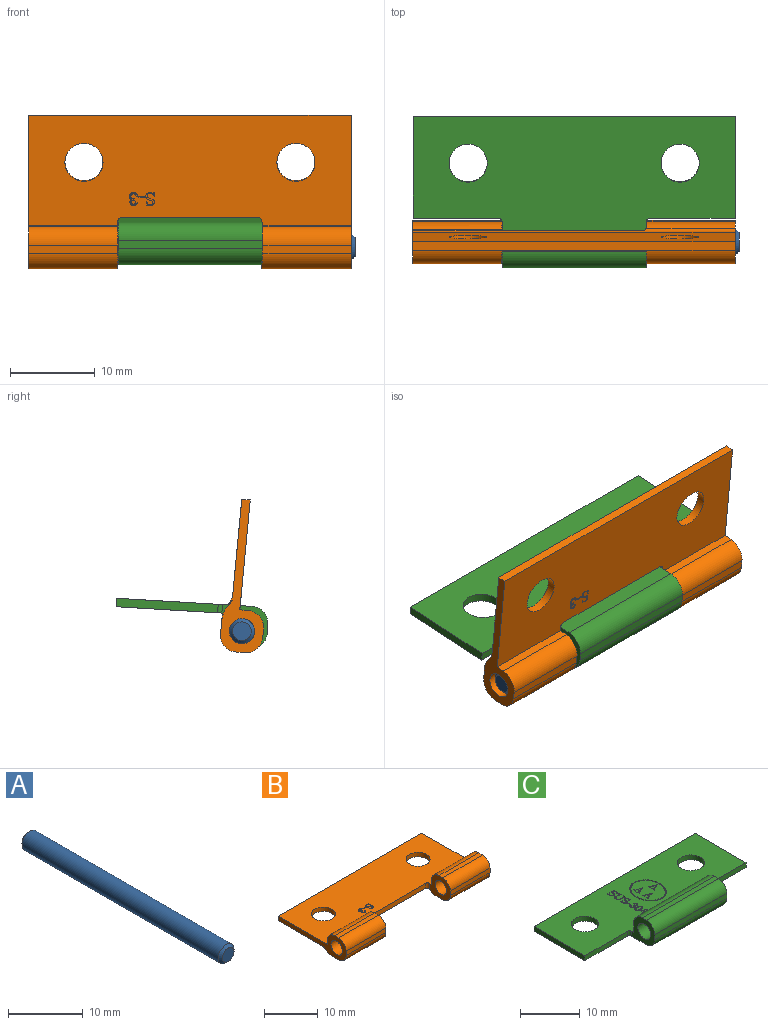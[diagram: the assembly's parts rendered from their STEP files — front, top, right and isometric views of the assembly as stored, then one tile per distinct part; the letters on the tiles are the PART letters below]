
ASSEMBLY  parts=3 mates=2
PART A: 5 faces, bbox 3x38x3 mm
  f0: cone r=1.3mm half-angle=45deg, axis (0,-1,0), area 4.6mm2, adj f1,f2
  f1: cylinder r=1.5mm len=37.2mm, axis (0,1,0), area 350.6mm2, adj f0,f3
  f2: plane 2.2x2.2mm, normal (0,1,0), area 3.8mm2, adj f0
  f3: cone r=1.3mm half-angle=45deg, axis (0,1,0), area 4.6mm2, adj f1,f4
  f4: plane 2.2x2.2mm, normal (0,-1,0), area 3.8mm2, adj f3
PART B: 86 faces, bbox 38x18x5 mm
  f0: extruded ~0.2x0.06mm, area 0mm2, adj f1,f7,f8,f83
  f1: plane 0.2x0.06mm, normal (-1,0,0), area 0mm2, adj f0,f2,f8,f83
  f2: extruded ~0.2x0.06mm, area 0mm2, adj f1,f3,f8,f83
  f3: plane 0.61x0.2mm, normal (0,-1,0), area 0.1mm2, adj f2,f4,f8,f83
  f4: extruded ~0.2x0.05mm, area 0mm2, adj f3,f5,f8,f83
  f5: plane 0.2x0.06mm, normal (1,0,0), area 0mm2, adj f4,f6,f8,f83
  f6: extruded ~0.2x0.05mm, area 0mm2, adj f5,f7,f8,f83
  f7: plane 0.63x0.2mm, normal (0,1,0), area 0.1mm2, adj f0,f6,f8,f83
  f8: plane 0.72x0.15mm, normal (0,0,1), area 0.1mm2, adj f0,f1,f2,f3,f4,f5,f6,f7
  f9: extruded ~0.33x0.2mm, area 0.1mm2, adj f10,f34,f35,f83
  f10: extruded ~0.47x0.38mm, area 0.1mm2, adj f9,f11,f35,f83
  f11: extruded ~0.44x0.42mm, area 0.1mm2, adj f10,f12,f35,f83
  f12: extruded ~0.42x0.36mm, area 0.1mm2, adj f11,f13,f35,f83
  f13: extruded ~0.33x0.31mm, area 0.1mm2, adj f12,f14,f35,f83
  f14: extruded ~0.49x0.44mm, area 0.1mm2, adj f13,f15,f35,f83
  f15: extruded ~0.2x0.03mm, area 0mm2, adj f14,f16,f35,f83
  f16: extruded ~0.2x0.02mm, area 0mm2, adj f15,f17,f35,f83
  f17: extruded ~0.48x0.2mm, area 0.1mm2, adj f16,f18,f35,f83
  f18: extruded ~0.2x0.04mm, area 0mm2, adj f17,f19,f35,f83
  f19: cylinder r=0.16mm len=0.2mm, axis (0,0,1), area 0mm2, adj f18,f20,f35,f83
  f20: extruded ~0.39x0.2mm, area 0.1mm2, adj f19,f21,f35,f83
  f21: extruded ~0.51x0.46mm, area 0.2mm2, adj f20,f22,f35,f83
  f22: extruded ~0.46x0.44mm, area 0.1mm2, adj f21,f23,f35,f83
  f23: extruded ~0.31x0.2mm, area 0.1mm2, adj f22,f24,f35,f83
  f24: extruded ~0.2x0.17mm, area 0mm2, adj f23,f25,f35,f83
  f25: extruded ~0.28x0.26mm, area 0.1mm2, adj f24,f26,f35,f83
  f26: extruded ~0.26x0.2mm, area 0.1mm2, adj f25,f27,f35,f83
  f27: cylinder r=0.62mm len=0.25mm, axis (0,0,1), area 0.1mm2, adj f26,f28,f35,f83
  f28: extruded ~0.2x0.02mm, area 0mm2, adj f27,f29,f35,f83
  f29: extruded ~0.2x0.03mm, area 0mm2, adj f28,f30,f35,f83
  f30: plane 0.21x0.2mm, normal (0.99,0.13,0), area 0mm2, adj f29,f31,f35,f83
  f31: bspline ~0.2x0.16mm, area 0mm2, adj f30,f32,f35,f83
  f32: extruded ~0.2x0.02mm, area 0mm2, adj f31,f33,f35,f83
  f33: extruded ~0.2x0.03mm, area 0mm2, adj f32,f34,f35,f83
  f34: extruded ~0.2x0.06mm, area 0mm2, adj f9,f33,f35,f83
  f35: plane 1.52x1.04mm, normal (0,0,1), area 0.5mm2, adj f9,f10,f11,f12,f13,f14,f15,f16
  f36: extruded ~0.48x0.42mm, area 0.1mm2, adj f37,f52,f53,f83
  f37: extruded ~0.51x0.47mm, area 0.2mm2, adj f36,f38,f53,f83
  f38: extruded ~0.37x0.28mm, area 0.1mm2, adj f37,f39,f53,f83
  f39: extruded ~0.3x0.21mm, area 0.1mm2, adj f38,f40,f53,f83
  f40: extruded ~0.44x0.39mm, area 0.1mm2, adj f39,f41,f53,f83
  f41: extruded ~0.45x0.39mm, area 0.1mm2, adj f40,f42,f53,f83
  f42: plane 0.2x0.18mm, normal (-0.18,-0.98,0), area 0mm2, adj f41,f43,f53,f83
  f43: extruded ~0.27x0.27mm, area 0.1mm2, adj f42,f44,f53,f83
  f44: extruded ~0.25x0.23mm, area 0.1mm2, adj f43,f45,f53,f83
  f45: extruded ~0.31x0.25mm, area 0.1mm2, adj f44,f46,f53,f83
  f46: cylinder r=0.38mm len=0.2mm, axis (0,0,1), area 0mm2, adj f45,f47,f53,f83
  f47: plane 0.2x0.16mm, normal (-0.99,0.12,0), area 0mm2, adj f46,f48,f53,f83
  f48: extruded ~0.2x0.13mm, area 0mm2, adj f47,f49,f53,f83
  f49: extruded ~0.29x0.29mm, area 0.1mm2, adj f48,f50,f53,f83
  f50: extruded ~0.31x0.31mm, area 0.1mm2, adj f49,f51,f53,f83
  f51: extruded ~0.3x0.29mm, area 0.1mm2, adj f50,f52,f53,f83
  f52: plane 0.2x0.18mm, normal (-0.13,0.99,0), area 0mm2, adj f36,f51,f53,f83
  f53: plane 1.53x0.98mm, normal (0,0,1), area 0.6mm2, adj f36,f37,f38,f39,f40,f41,f42,f43
  f54: cylinder r=3mm len=10.5mm, axis (1,0,0), area 22.1mm2, adj f55,f56,f57,f72,f81
  f55: plane 5.5x5mm, normal (1,0,0), area 15.9mm2, adj f54,f56,f68,f70,f72,f73,f75,f76
  f56: cylinder r=0.5mm len=1.32mm, axis (0,0,-1), area 0.9mm2, adj f54,f55,f57,f64,f83
  f57: cylinder r=2mm len=11mm, axis (1,0,0), area 5.9mm2, adj f54,f56,f64,f81
  f58: cylinder r=3mm len=10.5mm, axis (1,0,0), area 20.3mm2, adj f59,f60,f61,f63,f69
  f59: plane 10.5x1.73mm, normal (0,0,-1), area 18.2mm2, adj f58,f60,f69,f80
  f60: plane 18x5mm, normal (1,0,0), area 28.7mm2, adj f58,f59,f61,f62,f67,f71,f74,f77
  f61: cylinder r=2mm len=38mm, axis (-1,0,0), area 34.3mm2, adj f58,f60,f62,f63,f64,f81
  f62: plane 38x11.27mm, normal (0,0,-1), area 396.4mm2, adj f60,f61,f65,f66,f81,f84
  f63: cylinder r=0.5mm len=1.42mm, axis (0,0,-1), area 1mm2, adj f58,f61,f64,f69,f83
  f64: plane 27x1.14mm, normal (0,-1,0), area 19.7mm2, adj f56,f57,f61,f63,f81,f83
  f65: cylinder r=2.25mm len=4.5mm, axis (0,0,1), area 14.1mm2, adj f62,f83
  f66: cylinder r=2.25mm len=4.5mm, axis (0,0,1), area 14.1mm2, adj f62,f83
  f67: cylinder r=1.5mm len=10.5mm, axis (1,0,0), area 99mm2, adj f60,f69
  f68: cylinder r=1.5mm len=10.5mm, axis (1,0,0), area 99mm2, adj f55,f81
  f69: plane 5.5x5mm, normal (-1,0,0), area 16mm2, adj f58,f59,f63,f67,f71,f74,f77,f80
  f70: plane 10.5x1mm, normal (0,1,0), area 10.5mm2, adj f55,f73,f81,f83
  f71: plane 10.5x1mm, normal (0,1,0), area 10.5mm2, adj f60,f69,f74,f83
  f72: plane 10.5x1.6mm, normal (0,0,-1), area 16.8mm2, adj f54,f55,f75,f81
  f73: cylinder r=2mm len=10.5mm, axis (-1,0,0), area 33mm2, adj f55,f70,f76,f81
  f74: cylinder r=2mm len=10.5mm, axis (-1,0,0), area 33mm2, adj f60,f69,f71,f77
  f75: cylinder r=2mm len=10.5mm, axis (-1,0,0), area 33mm2, adj f55,f72,f78,f81
  f76: plane 10.5x1mm, normal (0,0,1), area 10.5mm2, adj f55,f73,f79,f81
  f77: plane 10.5x1mm, normal (0,0,1), area 10.5mm2, adj f60,f69,f74,f82
  f78: plane 10.5x1mm, normal (0,-1,0), area 10.5mm2, adj f55,f75,f79,f81
  f79: cylinder r=2mm len=10.5mm, axis (1,0,0), area 33mm2, adj f55,f76,f78,f81
  f80: cylinder r=2mm len=10.5mm, axis (-1,0,0), area 33mm2, adj f59,f60,f69,f85
  f81: plane 18x5mm, normal (-1,0,0), area 28.6mm2, adj f54,f57,f61,f62,f64,f68,f70,f72
  f82: cylinder r=2mm len=10.5mm, axis (1,0,0), area 33mm2, adj f60,f69,f77,f85
  f83: plane 38x13mm, normal (0,0,1), area 444.2mm2, adj f0,f1,f2,f3,f4,f5,f6,f7
  f84: plane 38x1mm, normal (0,1,0), area 38mm2, adj f60,f62,f81,f83
  f85: plane 10.5x1mm, normal (0,-1,0), area 10.5mm2, adj f60,f69,f80,f82
PART C: 246 faces, bbox 38.1x18.1x5.1 mm
  f0: extruded ~6.17x5.24mm, area 3.6mm2, adj f2,f221
  f1: extruded ~6.57x5.64mm, area 3.8mm2, adj f2,f3
  f2: plane 6.66x5.73mm, normal (0,0,1), area 3.7mm2, adj f0,f1
  f3: plane 38x13mm, normal (0,0,1), area 408mm2, adj f1,f7,f8,f9,f10,f11,f12,f13
  f4: plane 0.68x0.47mm, normal (0.57,0.82,0), area 0.2mm2, adj f5,f6,f18,f243
  f5: plane 0.47x0.2mm, normal (-1,0,0), area 0.1mm2, adj f4,f6,f18,f243
  f6: plane 0.68x0.2mm, normal (0,-1,0), area 0.1mm2, adj f4,f5,f18,f243
  f7: plane 0.2x0.18mm, normal (1,0,0), area 0mm2, adj f3,f8,f17,f18
  f8: plane 0.36x0.2mm, normal (0,1,0), area 0.1mm2, adj f3,f7,f9,f18
  f9: plane 0.2x0.2mm, normal (1,0,0), area 0mm2, adj f3,f8,f10,f18
  f10: plane 0.2x0.17mm, normal (0,1,0), area 0mm2, adj f3,f9,f11,f18
  f11: plane 0.2x0.2mm, normal (-1,0,0), area 0mm2, adj f3,f10,f12,f18
  f12: plane 0.97x0.2mm, normal (0,1,0), area 0.2mm2, adj f3,f11,f13,f18
  f13: plane 0.2x0.15mm, normal (-1,0,0), area 0mm2, adj f3,f12,f14,f18
  f14: plane 0.97x0.68mm, normal (-0.58,-0.82,0), area 0.2mm2, adj f3,f13,f15,f18
  f15: plane 0.2x0.17mm, normal (0,-1,0), area 0mm2, adj f3,f14,f16,f18
  f16: plane 0.65x0.2mm, normal (1,0,0), area 0.1mm2, adj f3,f15,f17,f18
  f17: plane 0.36x0.2mm, normal (0,-1,0), area 0.1mm2, adj f3,f7,f16,f18
  f18: plane 1.5x1.04mm, normal (0,0,1), area 0.6mm2, adj f4,f5,f6,f7,f8,f9,f10,f11
  f19: extruded ~0.61x0.3mm, area 0.2mm2, adj f20,f23,f29,f225
  f20: extruded ~0.61x0.3mm, area 0.2mm2, adj f19,f21,f29,f225
  f21: cylinder r=0.24mm len=0.2mm, axis (0,0,-1), area 0mm2, adj f20,f22,f29,f225
  f22: extruded ~0.51x0.2mm, area 0.1mm2, adj f21,f23,f29,f225
  f23: extruded ~0.61x0.3mm, area 0.2mm2, adj f19,f22,f29,f225
  f24: extruded ~0.61x0.2mm, area 0.1mm2, adj f3,f25,f28,f29
  f25: extruded ~0.34x0.2mm, area 0.1mm2, adj f3,f24,f26,f29
  f26: extruded ~0.77x0.49mm, area 0.2mm2, adj f3,f25,f27,f29
  f27: extruded ~0.77x0.49mm, area 0.2mm2, adj f3,f26,f28,f29
  f28: extruded ~0.77x0.49mm, area 0.2mm2, adj f3,f24,f27,f29
  f29: plane 1.53x0.98mm, normal (0,0,1), area 0.6mm2, adj f19,f20,f21,f22,f23,f24,f25,f26
  f30: extruded ~0.2x0.06mm, area 0mm2, adj f3,f31,f37,f38
  f31: plane 0.2x0.06mm, normal (0,-1,0), area 0mm2, adj f3,f30,f32,f38
  f32: extruded ~0.2x0.06mm, area 0mm2, adj f3,f31,f33,f38
  f33: plane 0.61x0.2mm, normal (1,0,0), area 0.1mm2, adj f3,f32,f34,f38
  f34: extruded ~0.2x0.05mm, area 0mm2, adj f3,f33,f35,f38
  f35: plane 0.2x0.06mm, normal (0,1,0), area 0mm2, adj f3,f34,f36,f38
  f36: extruded ~0.2x0.05mm, area 0mm2, adj f3,f35,f37,f38
  f37: plane 0.63x0.2mm, normal (-1,0,0), area 0.1mm2, adj f3,f30,f36,f38
  f38: plane 0.72x0.15mm, normal (0,0,1), area 0.1mm2, adj f30,f31,f32,f33,f34,f35,f36,f37
  f39: extruded ~0.2x0.05mm, area 0mm2, adj f3,f40,f57,f58
  f40: extruded ~0.2x0.04mm, area 0mm2, adj f3,f39,f41,f58
  f41: extruded ~0.61x0.2mm, area 0.1mm2, adj f3,f40,f42,f58
  f42: plane 0.31x0.2mm, normal (-0.02,-1,0), area 0.1mm2, adj f3,f41,f43,f58
  f43: extruded ~0.57x0.54mm, area 0.2mm2, adj f3,f42,f44,f58
  f44: extruded ~0.93x0.63mm, area 0.3mm2, adj f3,f43,f45,f58
  f45: extruded ~0.53x0.2mm, area 0.1mm2, adj f3,f44,f46,f58
  f46: extruded ~0.2x0.03mm, area 0mm2, adj f3,f45,f47,f58
  f47: extruded ~0.2x0.03mm, area 0mm2, adj f3,f46,f48,f58
  f48: plane 0.45x0.2mm, normal (-1,0,0), area 0.1mm2, adj f3,f47,f49,f58
  f49: extruded ~0.2x0.06mm, area 0mm2, adj f3,f48,f50,f58
  f50: extruded ~0.2x0.04mm, area 0mm2, adj f3,f49,f51,f58
  f51: extruded ~0.42x0.21mm, area 0.1mm2, adj f3,f50,f52,f58
  f52: extruded ~0.95x0.47mm, area 0.2mm2, adj f3,f51,f53,f58
  f53: extruded ~0.8x0.45mm, area 0.2mm2, adj f3,f52,f54,f58
  f54: extruded ~0.56x0.2mm, area 0.1mm2, adj f3,f53,f55,f58
  f55: extruded ~0.2x0.04mm, area 0mm2, adj f3,f54,f56,f58
  f56: extruded ~0.2x0.05mm, area 0mm2, adj f3,f55,f57,f58
  f57: plane 0.57x0.2mm, normal (-1,0,0), area 0.1mm2, adj f3,f39,f56,f58
  f58: plane 1.64x1.5mm, normal (0,0,1), area 0.5mm2, adj f39,f40,f41,f42,f43,f44,f45,f46
  f59: bspline ~0.2x0.17mm, area 0mm2, adj f60,f63,f88,f224
  f60: plane 0.32x0.2mm, normal (-1,0.02,0), area 0.1mm2, adj f59,f61,f88,f224
  f61: extruded ~0.31x0.2mm, area 0.1mm2, adj f60,f62,f88,f224
  f62: extruded ~0.31x0.2mm, area 0.1mm2, adj f61,f63,f88,f224
  f63: extruded ~0.62x0.25mm, area 0.1mm2, adj f59,f62,f88,f224
  f64: extruded ~0.72x0.29mm, area 0.2mm2, adj f65,f87,f88,f221
  f65: extruded ~0.75x0.41mm, area 0.2mm2, adj f64,f66,f88,f221
  f66: extruded ~0.2x0.03mm, area 0mm2, adj f65,f67,f88,f221
  f67: extruded ~0.2x0.04mm, area 0mm2, adj f66,f68,f88,f221
  f68: extruded ~0.25x0.2mm, area 0.1mm2, adj f67,f69,f88,f221
  f69: plane 0.22x0.2mm, normal (1,-0.03,0), area 0mm2, adj f68,f70,f88,f221
  f70: extruded ~0.2x0.02mm, area 0mm2, adj f69,f71,f88,f221
  f71: extruded ~0.2x0.04mm, area 0mm2, adj f70,f72,f88,f221
  f72: extruded ~0.2x0.17mm, area 0mm2, adj f71,f73,f88,f221
  f73: extruded ~0.4x0.2mm, area 0.1mm2, adj f72,f74,f88,f221
  f74: plane 0.53x0.2mm, normal (1,0.01,0), area 0.1mm2, adj f73,f75,f88,f221
  f75: plane 0.2x0.2mm, normal (0.32,-0.95,0), area 0mm2, adj f74,f76,f88,f221
  f76: extruded ~0.24x0.2mm, area 0.1mm2, adj f75,f77,f88,f221
  f77: extruded ~0.2x0.17mm, area 0mm2, adj f76,f78,f88,f221
  f78: extruded ~0.2x0.03mm, area 0mm2, adj f77,f79,f88,f221
  f79: extruded ~0.2x0.04mm, area 0mm2, adj f78,f80,f88,f221
  f80: extruded ~0.32x0.2mm, area 0.1mm2, adj f79,f81,f88,f221
  f81: extruded ~0.26x0.2mm, area 0.1mm2, adj f80,f82,f88,f221
  f82: plane 0.2x0.02mm, normal (1,-0.08,0), area 0mm2, adj f81,f83,f88,f221
  f83: extruded ~0.2x0.02mm, area 0mm2, adj f82,f84,f88,f221
  f84: extruded ~0.2x0.04mm, area 0mm2, adj f83,f85,f88,f221
  f85: extruded ~0.59x0.37mm, area 0.1mm2, adj f84,f86,f88,f221
  f86: extruded ~0.88x0.35mm, area 0.2mm2, adj f85,f87,f88,f221
  f87: plane 0.2x0.05mm, normal (-1,0,0), area 0mm2, adj f64,f86,f88,f221
  f88: plane 1.54x1.52mm, normal (0,0,1), area 0.5mm2, adj f59,f60,f61,f62,f63,f64,f65,f66
  f89: bspline ~0.2x0.17mm, area 0mm2, adj f90,f93,f118,f223
  f90: plane 0.32x0.2mm, normal (-1,0.02,0), area 0.1mm2, adj f89,f91,f118,f223
  f91: extruded ~0.31x0.2mm, area 0.1mm2, adj f90,f92,f118,f223
  f92: extruded ~0.31x0.2mm, area 0.1mm2, adj f91,f93,f118,f223
  f93: extruded ~0.62x0.25mm, area 0.1mm2, adj f89,f92,f118,f223
  f94: extruded ~0.72x0.29mm, area 0.2mm2, adj f95,f117,f118,f221
  f95: extruded ~0.75x0.41mm, area 0.2mm2, adj f94,f96,f118,f221
  f96: extruded ~0.2x0.03mm, area 0mm2, adj f95,f97,f118,f221
  f97: extruded ~0.2x0.04mm, area 0mm2, adj f96,f98,f118,f221
  f98: extruded ~0.25x0.2mm, area 0.1mm2, adj f97,f99,f118,f221
  f99: plane 0.22x0.2mm, normal (1,-0.03,0), area 0mm2, adj f98,f100,f118,f221
  f100: extruded ~0.2x0.02mm, area 0mm2, adj f99,f101,f118,f221
  f101: extruded ~0.2x0.04mm, area 0mm2, adj f100,f102,f118,f221
  f102: extruded ~0.2x0.17mm, area 0mm2, adj f101,f103,f118,f221
  f103: extruded ~0.4x0.2mm, area 0.1mm2, adj f102,f104,f118,f221
  f104: plane 0.53x0.2mm, normal (1,0.01,0), area 0.1mm2, adj f103,f105,f118,f221
  f105: plane 0.2x0.2mm, normal (0.32,-0.95,0), area 0mm2, adj f104,f106,f118,f221
  f106: extruded ~0.24x0.2mm, area 0.1mm2, adj f105,f107,f118,f221
  f107: extruded ~0.2x0.17mm, area 0mm2, adj f106,f108,f118,f221
  f108: extruded ~0.2x0.03mm, area 0mm2, adj f107,f109,f118,f221
  f109: extruded ~0.2x0.04mm, area 0mm2, adj f108,f110,f118,f221
  f110: extruded ~0.32x0.2mm, area 0.1mm2, adj f109,f111,f118,f221
  f111: extruded ~0.26x0.2mm, area 0.1mm2, adj f110,f112,f118,f221
  f112: plane 0.2x0.02mm, normal (1,-0.08,0), area 0mm2, adj f111,f113,f118,f221
  f113: extruded ~0.2x0.02mm, area 0mm2, adj f112,f114,f118,f221
  f114: extruded ~0.2x0.04mm, area 0mm2, adj f113,f115,f118,f221
  f115: extruded ~0.59x0.37mm, area 0.1mm2, adj f114,f116,f118,f221
  f116: extruded ~0.88x0.35mm, area 0.2mm2, adj f115,f117,f118,f221
  f117: plane 0.2x0.05mm, normal (-1,0,0), area 0mm2, adj f94,f116,f118,f221
  f118: plane 1.54x1.52mm, normal (0,0,1), area 0.5mm2, adj f89,f90,f91,f92,f93,f94,f95,f96
  f119: bspline ~0.2x0.17mm, area 0mm2, adj f120,f123,f148,f222
  f120: plane 0.32x0.2mm, normal (-1,0.02,0), area 0.1mm2, adj f119,f121,f148,f222
  f121: extruded ~0.31x0.2mm, area 0.1mm2, adj f120,f122,f148,f222
  f122: extruded ~0.31x0.2mm, area 0.1mm2, adj f121,f123,f148,f222
  f123: extruded ~0.62x0.25mm, area 0.1mm2, adj f119,f122,f148,f222
  f124: extruded ~0.72x0.29mm, area 0.2mm2, adj f125,f147,f148,f221
  f125: extruded ~0.75x0.41mm, area 0.2mm2, adj f124,f126,f148,f221
  f126: extruded ~0.2x0.03mm, area 0mm2, adj f125,f127,f148,f221
  f127: extruded ~0.2x0.04mm, area 0mm2, adj f126,f128,f148,f221
  f128: extruded ~0.25x0.2mm, area 0.1mm2, adj f127,f129,f148,f221
  f129: plane 0.22x0.2mm, normal (1,-0.03,0), area 0mm2, adj f128,f130,f148,f221
  f130: extruded ~0.2x0.02mm, area 0mm2, adj f129,f131,f148,f221
  f131: extruded ~0.2x0.04mm, area 0mm2, adj f130,f132,f148,f221
  f132: extruded ~0.2x0.17mm, area 0mm2, adj f131,f133,f148,f221
  f133: extruded ~0.4x0.2mm, area 0.1mm2, adj f132,f134,f148,f221
  f134: plane 0.53x0.2mm, normal (1,0.01,0), area 0.1mm2, adj f133,f135,f148,f221
  f135: plane 0.2x0.2mm, normal (0.32,-0.95,0), area 0mm2, adj f134,f136,f148,f221
  f136: extruded ~0.24x0.2mm, area 0.1mm2, adj f135,f137,f148,f221
  f137: extruded ~0.2x0.17mm, area 0mm2, adj f136,f138,f148,f221
  f138: extruded ~0.2x0.03mm, area 0mm2, adj f137,f139,f148,f221
  f139: extruded ~0.2x0.04mm, area 0mm2, adj f138,f140,f148,f221
  f140: extruded ~0.32x0.2mm, area 0.1mm2, adj f139,f141,f148,f221
  f141: extruded ~0.26x0.2mm, area 0.1mm2, adj f140,f142,f148,f221
  f142: plane 0.2x0.02mm, normal (1,-0.08,0), area 0mm2, adj f141,f143,f148,f221
  f143: extruded ~0.2x0.02mm, area 0mm2, adj f142,f144,f148,f221
  f144: extruded ~0.2x0.04mm, area 0mm2, adj f143,f145,f148,f221
  f145: extruded ~0.59x0.37mm, area 0.1mm2, adj f144,f146,f148,f221
  f146: extruded ~0.88x0.35mm, area 0.2mm2, adj f145,f147,f148,f221
  f147: plane 0.2x0.05mm, normal (-1,0,0), area 0mm2, adj f124,f146,f148,f221
  f148: plane 1.54x1.52mm, normal (0,0,1), area 0.5mm2, adj f119,f120,f121,f122,f123,f124,f125,f126
  f149: extruded ~0.33x0.2mm, area 0.1mm2, adj f3,f150,f174,f175
  f150: extruded ~0.47x0.38mm, area 0.1mm2, adj f3,f149,f151,f175
  f151: extruded ~0.44x0.42mm, area 0.1mm2, adj f3,f150,f152,f175
  f152: extruded ~0.42x0.36mm, area 0.1mm2, adj f3,f151,f153,f175
  f153: extruded ~0.33x0.31mm, area 0.1mm2, adj f3,f152,f154,f175
  f154: extruded ~0.49x0.44mm, area 0.1mm2, adj f3,f153,f155,f175
  f155: extruded ~0.2x0.03mm, area 0mm2, adj f3,f154,f156,f175
  f156: extruded ~0.2x0.02mm, area 0mm2, adj f3,f155,f157,f175
  f157: extruded ~0.48x0.2mm, area 0.1mm2, adj f3,f156,f158,f175
  f158: extruded ~0.2x0.04mm, area 0mm2, adj f3,f157,f159,f175
  f159: cylinder r=0.16mm len=0.2mm, axis (0,0,1), area 0mm2, adj f3,f158,f160,f175
  f160: extruded ~0.39x0.2mm, area 0.1mm2, adj f3,f159,f161,f175
  f161: extruded ~0.51x0.46mm, area 0.2mm2, adj f3,f160,f162,f175
  f162: extruded ~0.46x0.44mm, area 0.1mm2, adj f3,f161,f163,f175
  f163: extruded ~0.31x0.2mm, area 0.1mm2, adj f3,f162,f164,f175
  f164: extruded ~0.2x0.17mm, area 0mm2, adj f3,f163,f165,f175
  f165: extruded ~0.28x0.26mm, area 0.1mm2, adj f3,f164,f166,f175
  f166: extruded ~0.26x0.2mm, area 0.1mm2, adj f3,f165,f167,f175
  f167: cylinder r=0.62mm len=0.25mm, axis (0,0,1), area 0.1mm2, adj f3,f166,f168,f175
  f168: extruded ~0.2x0.02mm, area 0mm2, adj f3,f167,f169,f175
  f169: extruded ~0.2x0.03mm, area 0mm2, adj f3,f168,f170,f175
  f170: plane 0.21x0.2mm, normal (-0.13,0.99,0), area 0mm2, adj f3,f169,f171,f175
  f171: bspline ~0.2x0.16mm, area 0mm2, adj f3,f170,f172,f175
  f172: extruded ~0.2x0.02mm, area 0mm2, adj f3,f171,f173,f175
  f173: extruded ~0.2x0.03mm, area 0mm2, adj f3,f172,f174,f175
  f174: extruded ~0.2x0.06mm, area 0mm2, adj f3,f149,f173,f175
  f175: plane 1.52x1.04mm, normal (0,0,1), area 0.5mm2, adj f149,f150,f151,f152,f153,f154,f155,f156
  f176: extruded ~0.33x0.2mm, area 0.1mm2, adj f3,f177,f201,f202
  f177: extruded ~0.47x0.38mm, area 0.1mm2, adj f3,f176,f178,f202
  f178: extruded ~0.44x0.42mm, area 0.1mm2, adj f3,f177,f179,f202
  f179: extruded ~0.42x0.36mm, area 0.1mm2, adj f3,f178,f180,f202
  f180: extruded ~0.33x0.31mm, area 0.1mm2, adj f3,f179,f181,f202
  f181: extruded ~0.49x0.44mm, area 0.1mm2, adj f3,f180,f182,f202
  f182: extruded ~0.2x0.03mm, area 0mm2, adj f3,f181,f183,f202
  f183: extruded ~0.2x0.02mm, area 0mm2, adj f3,f182,f184,f202
  f184: extruded ~0.48x0.2mm, area 0.1mm2, adj f3,f183,f185,f202
  f185: extruded ~0.2x0.04mm, area 0mm2, adj f3,f184,f186,f202
  f186: cylinder r=0.16mm len=0.2mm, axis (0,0,1), area 0mm2, adj f3,f185,f187,f202
  f187: extruded ~0.39x0.2mm, area 0.1mm2, adj f3,f186,f188,f202
  f188: extruded ~0.51x0.46mm, area 0.2mm2, adj f3,f187,f189,f202
  f189: extruded ~0.46x0.44mm, area 0.1mm2, adj f3,f188,f190,f202
  f190: extruded ~0.31x0.2mm, area 0.1mm2, adj f3,f189,f191,f202
  f191: extruded ~0.2x0.17mm, area 0mm2, adj f3,f190,f192,f202
  f192: extruded ~0.28x0.26mm, area 0.1mm2, adj f3,f191,f193,f202
  f193: extruded ~0.26x0.2mm, area 0.1mm2, adj f3,f192,f194,f202
  f194: cylinder r=0.62mm len=0.25mm, axis (0,0,1), area 0.1mm2, adj f3,f193,f195,f202
  f195: extruded ~0.2x0.02mm, area 0mm2, adj f3,f194,f196,f202
  f196: extruded ~0.2x0.03mm, area 0mm2, adj f3,f195,f197,f202
  f197: plane 0.21x0.2mm, normal (-0.13,0.99,0), area 0mm2, adj f3,f196,f198,f202
  f198: bspline ~0.2x0.16mm, area 0mm2, adj f3,f197,f199,f202
  f199: extruded ~0.2x0.02mm, area 0mm2, adj f3,f198,f200,f202
  f200: extruded ~0.2x0.03mm, area 0mm2, adj f3,f199,f201,f202
  f201: extruded ~0.2x0.06mm, area 0mm2, adj f3,f176,f200,f202
  f202: plane 1.52x1.04mm, normal (0,0,1), area 0.5mm2, adj f176,f177,f178,f179,f180,f181,f182,f183
  f203: extruded ~0.48x0.42mm, area 0.1mm2, adj f3,f204,f219,f220
  f204: extruded ~0.51x0.47mm, area 0.2mm2, adj f3,f203,f205,f220
  f205: extruded ~0.37x0.28mm, area 0.1mm2, adj f3,f204,f206,f220
  f206: extruded ~0.3x0.21mm, area 0.1mm2, adj f3,f205,f207,f220
  f207: extruded ~0.44x0.39mm, area 0.1mm2, adj f3,f206,f208,f220
  f208: extruded ~0.45x0.39mm, area 0.1mm2, adj f3,f207,f209,f220
  f209: plane 0.2x0.18mm, normal (0.98,-0.18,0), area 0mm2, adj f3,f208,f210,f220
  f210: extruded ~0.27x0.27mm, area 0.1mm2, adj f3,f209,f211,f220
  f211: extruded ~0.25x0.23mm, area 0.1mm2, adj f3,f210,f212,f220
  f212: extruded ~0.31x0.25mm, area 0.1mm2, adj f3,f211,f213,f220
  f213: cylinder r=0.38mm len=0.2mm, axis (0,0,1), area 0mm2, adj f3,f212,f214,f220
  f214: plane 0.2x0.16mm, normal (-0.12,-0.99,0), area 0mm2, adj f3,f213,f215,f220
  f215: extruded ~0.2x0.13mm, area 0mm2, adj f3,f214,f216,f220
  f216: extruded ~0.29x0.29mm, area 0.1mm2, adj f3,f215,f217,f220
  f217: extruded ~0.31x0.31mm, area 0.1mm2, adj f3,f216,f218,f220
  f218: extruded ~0.3x0.29mm, area 0.1mm2, adj f3,f217,f219,f220
  f219: plane 0.2x0.18mm, normal (-0.99,-0.13,0), area 0mm2, adj f3,f203,f218,f220
  f220: plane 1.53x0.98mm, normal (0,0,1), area 0.6mm2, adj f203,f204,f205,f206,f207,f208,f209,f210
  f221: plane 6.26x5.33mm, normal (0,0,1), area 23.5mm2, adj f0,f64,f65,f66,f67,f68,f69,f70
  f222: plane 0.62x0.49mm, normal (0,0,1), area 0.2mm2, adj f119,f120,f121,f122,f123
  f223: plane 0.62x0.49mm, normal (0,0,1), area 0.2mm2, adj f89,f90,f91,f92,f93
  f224: plane 0.62x0.49mm, normal (0,0,1), area 0.2mm2, adj f59,f60,f61,f62,f63
  f225: plane 1.23x0.6mm, normal (0,0,1), area 0.6mm2, adj f19,f20,f21,f22,f23
  f226: cylinder r=0.5mm len=1mm, axis (0,0,-1), area 0.8mm2, adj f3,f227,f234,f240
  f227: plane 5.5x5mm, normal (1,0,0), area 15.9mm2, adj f3,f226,f232,f236,f237,f238,f239,f240
  f228: cylinder r=0.5mm len=1mm, axis (0,0,-1), area 0.8mm2, adj f3,f229,f233,f240
  f229: plane 10x1mm, normal (0,-1,0), area 10mm2, adj f3,f228,f240,f241
  f230: cylinder r=2.25mm len=4.5mm, axis (0,0,1), area 14.1mm2, adj f3,f240
  f231: cylinder r=2.25mm len=4.5mm, axis (0,0,1), area 14.1mm2, adj f3,f240
  f232: cylinder r=1.5mm len=17mm, axis (1,0,0), area 160.2mm2, adj f227,f233
  f233: plane 5.5x5mm, normal (-1,0,0), area 15.9mm2, adj f3,f228,f232,f236,f237,f238,f239,f240
  f234: plane 10x1mm, normal (0,-1,0), area 10mm2, adj f3,f226,f235,f240
  f235: plane 12x1mm, normal (1,0,0), area 12mm2, adj f3,f234,f240,f245
  f236: plane 17x2mm, normal (0,1,0), area 34mm2, adj f3,f227,f233,f237
  f237: cylinder r=2mm len=17mm, axis (-1,0,0), area 53.4mm2, adj f227,f233,f236,f238
  f238: plane 17x1mm, normal (0,0,1), area 17mm2, adj f227,f233,f237,f242
  f239: cylinder r=2mm len=17mm, axis (-1,0,0), area 53.4mm2, adj f227,f233,f240,f244
  f240: plane 38x16mm, normal (0,0,-1), area 492.3mm2, adj f226,f227,f228,f229,f230,f231,f233,f234
  f241: plane 12x1mm, normal (-1,0,0), area 12mm2, adj f3,f229,f240,f245
  f242: cylinder r=2mm len=17mm, axis (1,0,0), area 53.4mm2, adj f227,f233,f238,f244
  f243: plane 0.68x0.47mm, normal (0,0,1), area 0.2mm2, adj f4,f5,f6
  f244: plane 17x1mm, normal (0,-1,0), area 17mm2, adj f227,f233,f239,f242
  f245: plane 38x1mm, normal (0,1,0), area 38mm2, adj f3,f235,f240,f241
PLACE A rot(axis=(0.59,0.59,-0.54),123.2deg) t=(-18.75,-58.26,8.1)mm
PLACE B rot(axis=(1,0,0),95.4deg) t=(-0.24,-56.38,14.81)mm
PLACE C rot(axis=(0,-1,-0.03),180deg) t=(-0.22,-52.45,11.46)mm
MATE revolute B.f67 <-> A.f0  axis (1,0,0) through (-19.24,-58.26,8.1)mm
MATE revolute A.f0 <-> C.f237  axis (1,0,0) through (19.25,-58.26,8.1)mm
